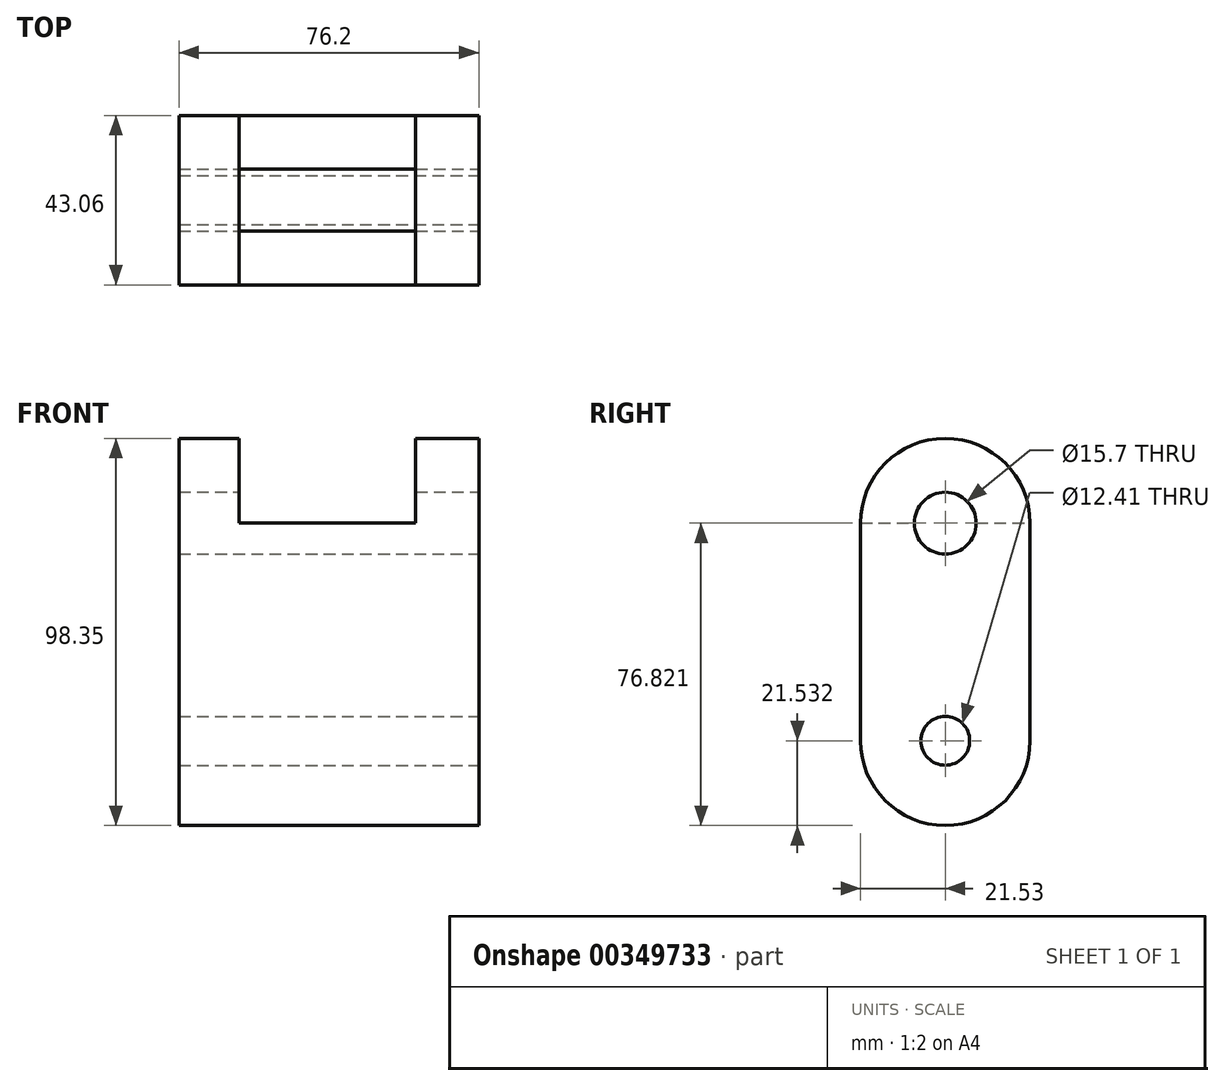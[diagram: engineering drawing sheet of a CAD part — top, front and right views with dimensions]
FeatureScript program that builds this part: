
annotation { "Feature Type Name" : "Feature", "Feature Type Description" : "" }
export const myFeature = defineFeature(function(context is Context, id is Id, definition is map)
    precondition{}
    {
        {
            var Q0;
            Q0=qCreatedBy(makeId("Right.planeOp"),FACE);
            var sketch = newSketch(context, id + "F0", { "sketchPlane" : qUnion([Q0])});
            skLineSegment(sketch, "E0", {"start": v(-21.53, -22.33) * mm, "end": v(-21.53, 32.96) * mm});
            skLineSegment(sketch, "E1", {"start": v(21.53, 32.96) * mm, "end": v(21.53, -22.33) * mm});
            skArc(sketch, "E2", {"start": v(-21.53, 32.96) * mm, "mid": v(0, 54.5) * mm, "end": v(21.53, 32.96) * mm});
            skArc(sketch, "E3", {"start": v(-21.53, -22.33) * mm, "mid": v(0, -43.86) * mm, "end": v(21.53, -22.33) * mm});
            skSolve(sketch);
        }
        {
            var Q0;
            Q0 = qSketchRegion(id + "F0", true);
            extrude(context, id + "F1", {"entities" : qUnion([Q0]), "depth" : 38.1 * mm, "hasSecondDirection" : true, "secondDirectionOppositeDirection" : true, "secondDirectionDepth" : 38.1 * mm});
        }
        {
            var Q0;
            Q0=makeQuery(id+"F1.opExtrude","CAP_FACE",FACE,{"disambiguationData":[OSD([sQuery(id+"F0.wireOp",EDGE,"E0"),sQuery(id+"F0.wireOp",EDGE,"E1"),sQuery(id+"F0.wireOp",EDGE,"E2"),sQuery(id+"F0.wireOp",EDGE,"E3")])],"isStart":false});
            var sketch = newSketch(context, id + "F2", { "sketchPlane" : qUnion([Q0])});
            skArc(sketch, "E4.0", {"start": v(-21.53, 32.96) * mm, "mid": v(0, 54.5) * mm, "end": v(21.53, 32.96) * mm});
            skArc(sketch, "E5.0", {"start": v(-21.53, -22.33) * mm, "mid": v(0, -43.86) * mm, "end": v(21.53, -22.33) * mm});
            skCircle(sketch, "E6", {"center": v(0, 32.96) * mm, "radius": 7.85 * mm});
            skCircle(sketch, "E7", {"center": v(0, -22.33) * mm, "radius": 6.2 * mm});
            skSolve(sketch);
        }
        {
            var Q0;
            Q0=makeQuery(id+"F2.imprint","IMPRINT",FACE,{"disambiguationData":[TD([[makeQuery(id+"F2.imprint","IMPRINT",EDGE,{"derivedFrom":sQuery(id+"F2.wireOp",EDGE,"E6")}),1.0]])]});
            var Q1;
            Q1=makeQuery(id+"F2.imprint","IMPRINT",FACE,{"disambiguationData":[TD([[makeQuery(id+"F2.imprint","IMPRINT",EDGE,{"derivedFrom":sQuery(id+"F2.wireOp",EDGE,"E7")}),1.0]])]});
            extrude(context, id + "F3", {"entities" : qUnion([Q0, Q1]), "operationType" : NewBodyOperationType.REMOVE, "endBound" : BoundingType.THROUGH_ALL, "oppositeDirection" : true, "depth" : 25.4 * mm});
        }
        {
            var Q0;
            Q0=makeQuery(id+"F1.opExtrude","SWEPT_FACE",FACE,{"disambiguationData":[OSD([sQuery(id+"F0.wireOp",EDGE,"E1")])]});
            var sketch = newSketch(context, id + "F4", { "sketchPlane" : qUnion([Q0])});
            skLineSegment(sketch, "E8.0", {"start": v(-38.1, -22.33) * mm, "end": v(38.1, -22.33) * mm});
            skLineSegment(sketch, "E9.bottom", {"start": v(-22.06, -22.33) * mm, "end": v(22.86, -22.33) * mm});
            skLineSegment(sketch, "E9.top", {"start": v(-22.06, 69.11) * mm, "end": v(22.86, 69.11) * mm});
            skLineSegment(sketch, "E9.left", {"start": v(-22.06, -22.33) * mm, "end": v(-22.06, 69.11) * mm});
            skLineSegment(sketch, "E9.right", {"start": v(22.86, -22.33) * mm, "end": v(22.86, 69.11) * mm});
            skSolve(sketch);
        }
        {
            var Q0;
            {var subQ0=sQuery(id+"F4.wireOp",EDGE,"E9.top");Q0=makeQuery(id+"F4.imprint","IMPRINT",FACE,{"disambiguationData":[TD([[makeQuery(id+"F4.imprint","IMPRINT",EDGE,{"derivedFrom":subQ0}),-1.0]])]});}
            var Q1;
            {var subQ0=sQuery(id+"F4.wireOp",EDGE,"E9.bottom");Q1=makeQuery(id+"F4.imprint","IMPRINT",FACE,{"disambiguationData":[TD([[makeQuery(id+"F4.imprint","IMPRINT",EDGE,{"derivedFrom":subQ0}),1.0]])]});}
            extrude(context, id + "F5", {"entities" : qUnion([Q0, Q1]), "operationType" : NewBodyOperationType.REMOVE, "endBound" : BoundingType.THROUGH_ALL, "oppositeDirection" : true, "depth" : 25.4 * mm});
        }
        {
            var Q0;
            Q0=makeQuery(id+"F5.boolean.opBoolean","COPY",FACE,{"derivedFrom":makeQuery(id+"F5.opExtrude","SWEPT_FACE",FACE,{"disambiguationData":[OSD([sQuery(id+"F4.wireOp",EDGE,"E9.right")])]})});
            var sketch = newSketch(context, id + "F6", { "sketchPlane" : qUnion([Q0])});
            skArc(sketch, "E10.0", {"start": v(-21.53, -22.33) * mm, "mid": v(0, -43.86) * mm, "end": v(21.53, -22.33) * mm});
            skCircle(sketch, "E11", {"center": v(0, -22.33) * mm, "radius": 21.53 * mm});
            skCircle(sketch, "E12.0", {"center": v(0, -22.33) * mm, "radius": 6.2 * mm});
            skSolve(sketch);
        }
        {
            var Q0;
            Q0 = qSketchRegion(id + "F6", true);
            extrude(context, id + "F7", {"entities" : qUnion([Q0]), "operationType" : NewBodyOperationType.ADD, "endBound" : BoundingType.UP_TO_NEXT, "depth" : 25.4 * mm});
        }
    });
